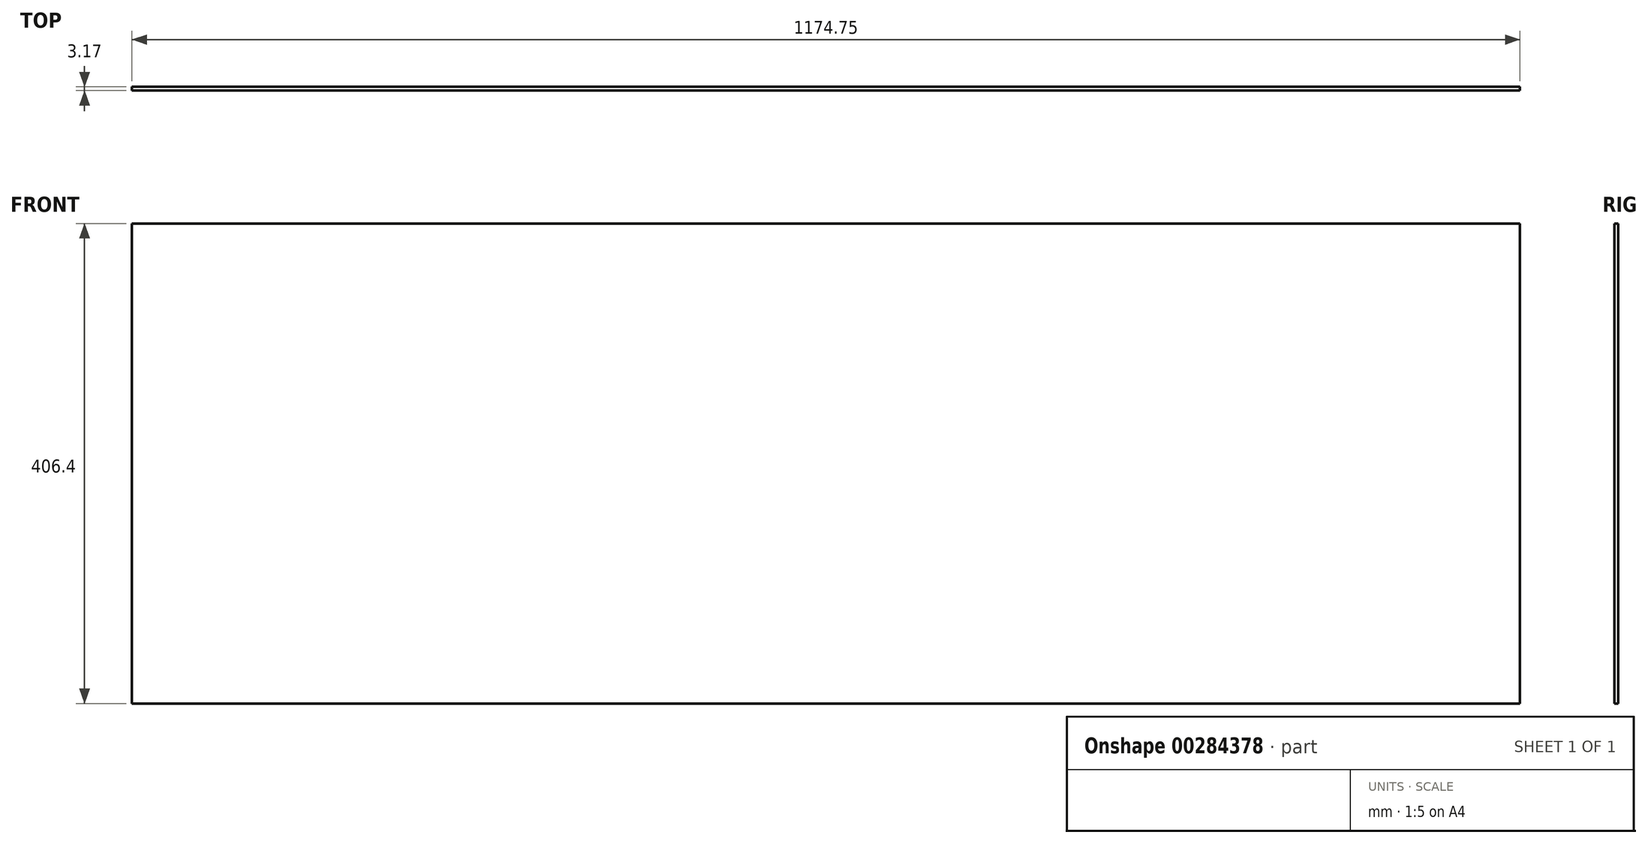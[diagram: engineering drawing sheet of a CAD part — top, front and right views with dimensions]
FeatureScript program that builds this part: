
annotation { "Feature Type Name" : "Feature", "Feature Type Description" : "" }
export const myFeature = defineFeature(function(context is Context, id is Id, definition is map)
    precondition{}
    {
        {
            var Q0;
            Q0=qCreatedBy(makeId("Front.planeOp"),FACE);
            var sketch = newSketch(context, id + "F0", { "sketchPlane" : qUnion([Q0])});
            skLineSegment(sketch, "E0.bottom", {"start": v(0, 0) * mm, "end": v(1174.75, 0) * mm});
            skLineSegment(sketch, "E0.top", {"start": v(0, 406.4) * mm, "end": v(1174.75, 406.4) * mm});
            skLineSegment(sketch, "E0.left", {"start": v(0, 0) * mm, "end": v(0, 406.4) * mm});
            skLineSegment(sketch, "E0.right", {"start": v(1174.75, 0) * mm, "end": v(1174.75, 406.4) * mm});
            skSolve(sketch);
        }
        {
            var Q0;
            Q0 = qSketchRegion(id + "F0", true);
            extrude(context, id + "F1", {"entities" : qUnion([Q0]), "depth" : 3.17 * mm});
        }
    });
